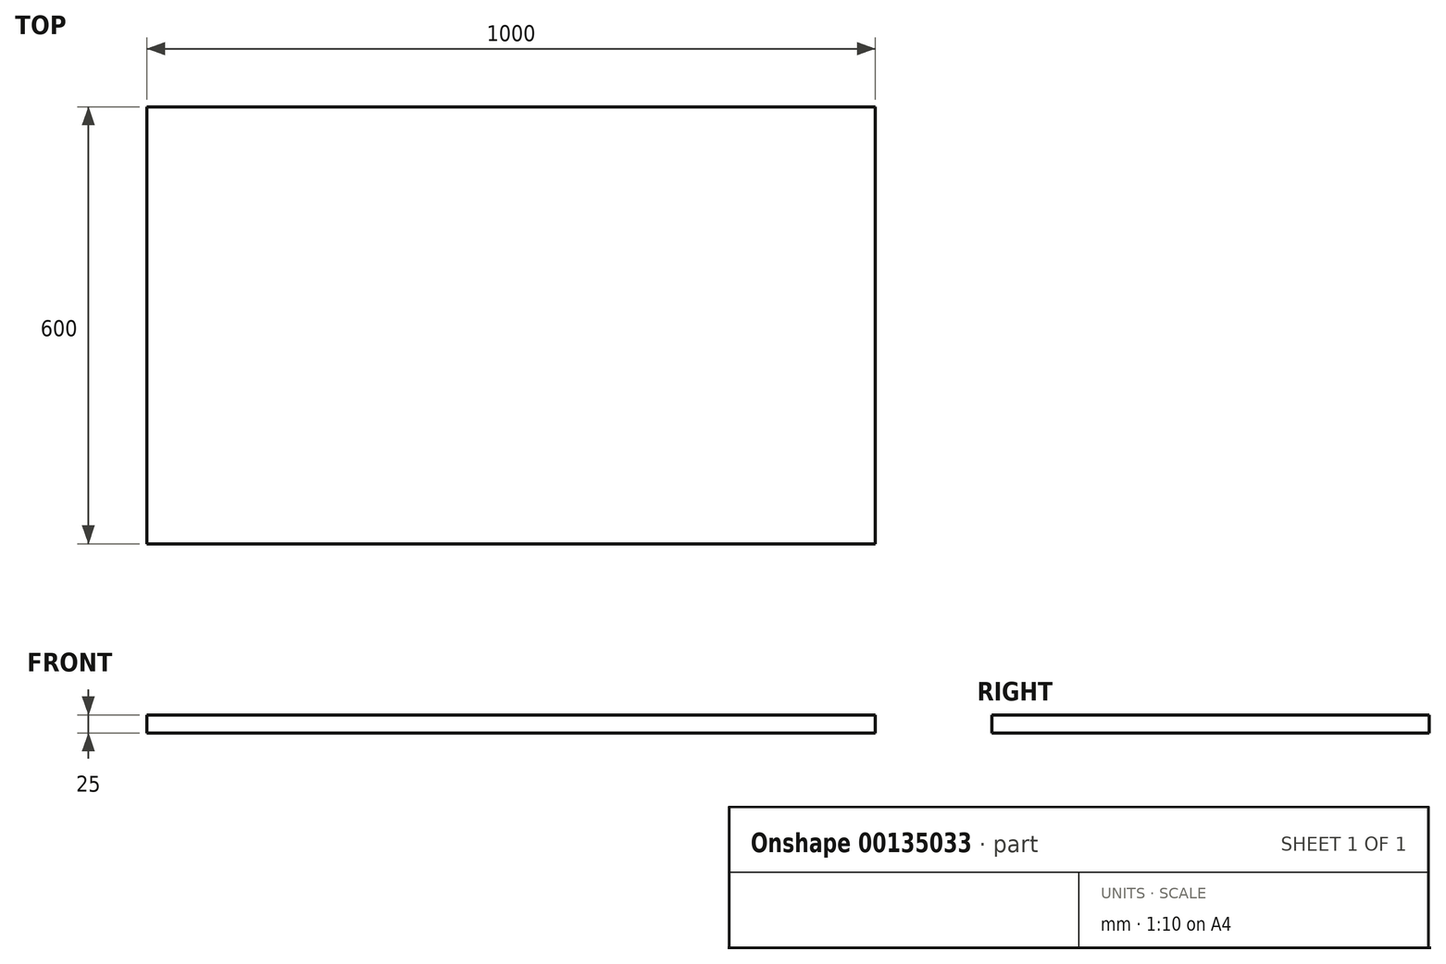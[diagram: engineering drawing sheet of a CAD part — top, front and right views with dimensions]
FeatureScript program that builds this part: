
annotation { "Feature Type Name" : "Feature", "Feature Type Description" : "" }
export const myFeature = defineFeature(function(context is Context, id is Id, definition is map)
    precondition{}
    {
        {
            var Q0;
            Q0=qCreatedBy(makeId("Top.planeOp"),FACE);
            var sketch = newSketch(context, id + "F0", { "sketchPlane" : qUnion([Q0])});
            skLineSegment(sketch, "E0.bottom", {"start": v(500, -299.49) * mm, "end": v(-500, -299.49) * mm});
            skLineSegment(sketch, "E0.top", {"start": v(500, 300.51) * mm, "end": v(-500, 300.51) * mm});
            skLineSegment(sketch, "E0.left", {"start": v(500, -299.49) * mm, "end": v(500, 300.51) * mm});
            skLineSegment(sketch, "E0.right", {"start": v(-500, -299.49) * mm, "end": v(-500, 300.51) * mm});
            skPoint(sketch, "E0.middle", {"position": v(0, 0.51) * mm});
            skSolve(sketch);
        }
        {
            var Q0;
            Q0 = qSketchRegion(id + "F0", true);
            extrude(context, id + "F1", {"entities" : qUnion([Q0]), "depth" : 25 * mm});
        }
    });
